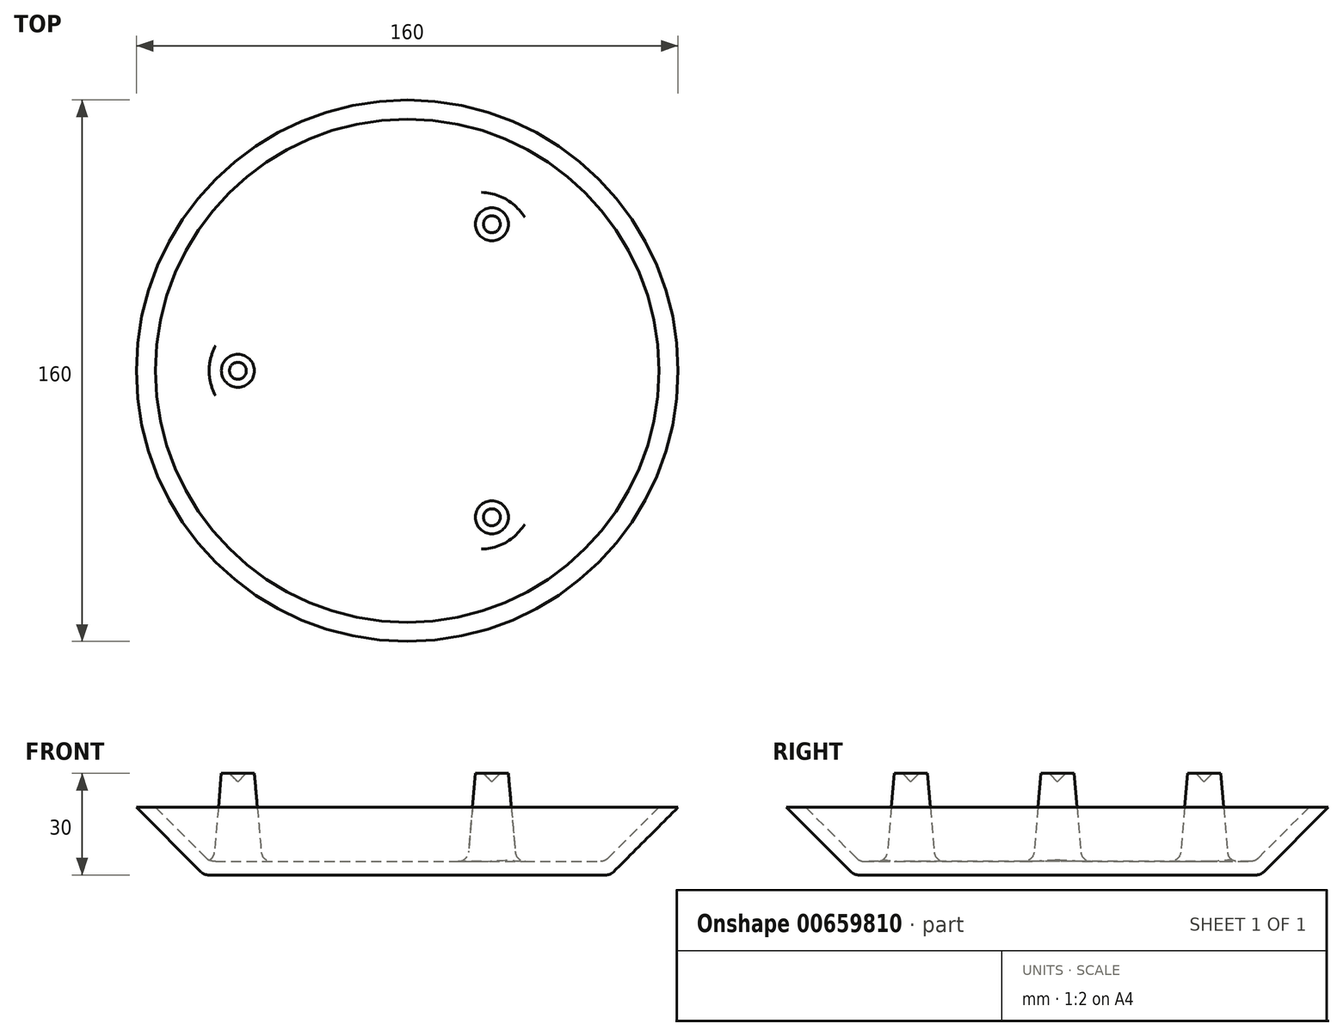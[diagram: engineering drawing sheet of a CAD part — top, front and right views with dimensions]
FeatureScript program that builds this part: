
annotation { "Feature Type Name" : "Feature", "Feature Type Description" : "" }
export const myFeature = defineFeature(function(context is Context, id is Id, definition is map)
    precondition{}
    {
        {
            var Q0;
            Q0=qCreatedBy(makeId("Front.planeOp"),FACE);
            var sketch = newSketch(context, id + "F0", { "sketchPlane" : qUnion([Q0])});
            skLineSegment(sketch, "E0", {"start": v(0, 0) * mm, "end": v(60, 0) * mm});
            skLineSegment(sketch, "E1", {"start": v(60, 0) * mm, "end": v(80, 20) * mm});
            skLineSegment(sketch, "E2", {"start": v(80, 20) * mm, "end": v(74.34, 20) * mm});
            skLineSegment(sketch, "E3", {"start": v(74.34, 20) * mm, "end": v(58.34, 4) * mm});
            skLineSegment(sketch, "E4", {"start": v(58.34, 4) * mm, "end": v(0, 4) * mm});
            skLineSegment(sketch, "E5", {"start": v(0, 4) * mm, "end": v(0, 0) * mm});
            skSolve(sketch);
        }
        {
            var Q0;
            Q0 = qSketchRegion(id + "F0", true);
            var Q1;
            Q1=sQuery(id+"F0.wireOp",EDGE,"E5");
            revolve(context, id + "F1", {"entities" : qUnion([Q0]), "axis" : qUnion([Q1]), "revolveType" : RevolveType.FULL});
        }
        {
            var Q0;
            Q0=qCreatedBy(makeId("Top.planeOp"),FACE);
            var sketch = newSketch(context, id + "F2", { "sketchPlane" : qUnion([Q0])});
            skCircle(sketch, "E6", {"center": v(25, 43.3) * mm, "radius": 7.5 * mm});
            skCircle(sketch, "E7", {"center": v(-50, 0) * mm, "radius": 7.5 * mm});
            skLineSegment(sketch, "E8", {"start": v(0, 0) * mm, "end": v(31.77, 55.03) * mm, "construction": true});
            skLineSegment(sketch, "E9", {"start": v(0, 0) * mm, "end": v(26.35, -45.65) * mm, "construction": true});
            skCircle(sketch, "E10", {"center": v(25, -43.3) * mm, "radius": 7.5 * mm});
            skSolve(sketch);
        }
        {
            var Q0;
            Q0 = qSketchRegion(id + "F2", true);
            var Q1;
            Q1=makeQuery(id+"F1.opRevolve","SWEPT_FACE",FACE,{"disambiguationData":[OSD([sQuery(id+"F0.wireOp",EDGE,"E2")])]});
            extrude(context, id + "F3", {"entities" : qUnion([Q0]), "operationType" : NewBodyOperationType.ADD, "depth" : 30 * mm, "endBoundEntityFace" : qUnion([Q1]), "offsetDistance" : 10 * mm, "hasDraft" : true, "draftAngle" : 5 * degree, "draftPullDirection" : true});
        }
        {
            var Q0;
            Q0=makeQuery(id+"F1.opRevolve","SWEPT_FACE",FACE,{"disambiguationData":[OSD([sQuery(id+"F0.wireOp",EDGE,"E4")])]});
            fillet(context, id + "F4", {"entities" : qUnion([Q0]), "radius" : 3 * mm, "tangentPropagation" : true, "allowEdgeOverflow" : false});
        }
        {
            var Q0;
            Q0=makeQuery(id+"F1.opRevolve","SWEPT_FACE",FACE,{"disambiguationData":[OSD([sQuery(id+"F0.wireOp",EDGE,"E0")])]});
            fillet(context, id + "F5", {"entities" : qUnion([Q0]), "radius" : 3 * mm, "tangentPropagation" : true, "allowEdgeOverflow" : false});
        }
        {
            var Q0;
            Q0=makeQuery(id+"F3.opExtrude","CAP_FACE",FACE,{"disambiguationData":[OSD([sQuery(id+"F2.wireOp",EDGE,"E7")])],"isStart":false});
            var sketch = newSketch(context, id + "F6", { "sketchPlane" : qUnion([Q0])});
            skCircle(sketch, "E11.0.0", {"center": v(-50, 0) * mm, "radius": 4.88 * mm, "construction": true});
            skCircle(sketch, "E12.0", {"center": v(25, 43.3) * mm, "radius": 4.88 * mm, "construction": true});
            skCircle(sketch, "E13.0", {"center": v(25, -43.3) * mm, "radius": 4.88 * mm, "construction": true});
            skCircle(sketch, "E14", {"center": v(25, 43.3) * mm, "radius": 2.5 * mm});
            skCircle(sketch, "E15", {"center": v(25, -43.3) * mm, "radius": 2.5 * mm});
            skCircle(sketch, "E16", {"center": v(-50, 0) * mm, "radius": 2.5 * mm});
            skSolve(sketch);
        }
        {
            var Q0;
            Q0 = qSketchRegion(id + "F6", true);
            extrude(context, id + "F7", {"entities" : qUnion([Q0]), "operationType" : NewBodyOperationType.REMOVE, "oppositeDirection" : true, "depth" : 2.5 * mm, "offsetDistance" : 25 * mm, "hasDraft" : true, "draftAngle" : 45 * degree, "draftPullDirection" : true});
        }
    });
